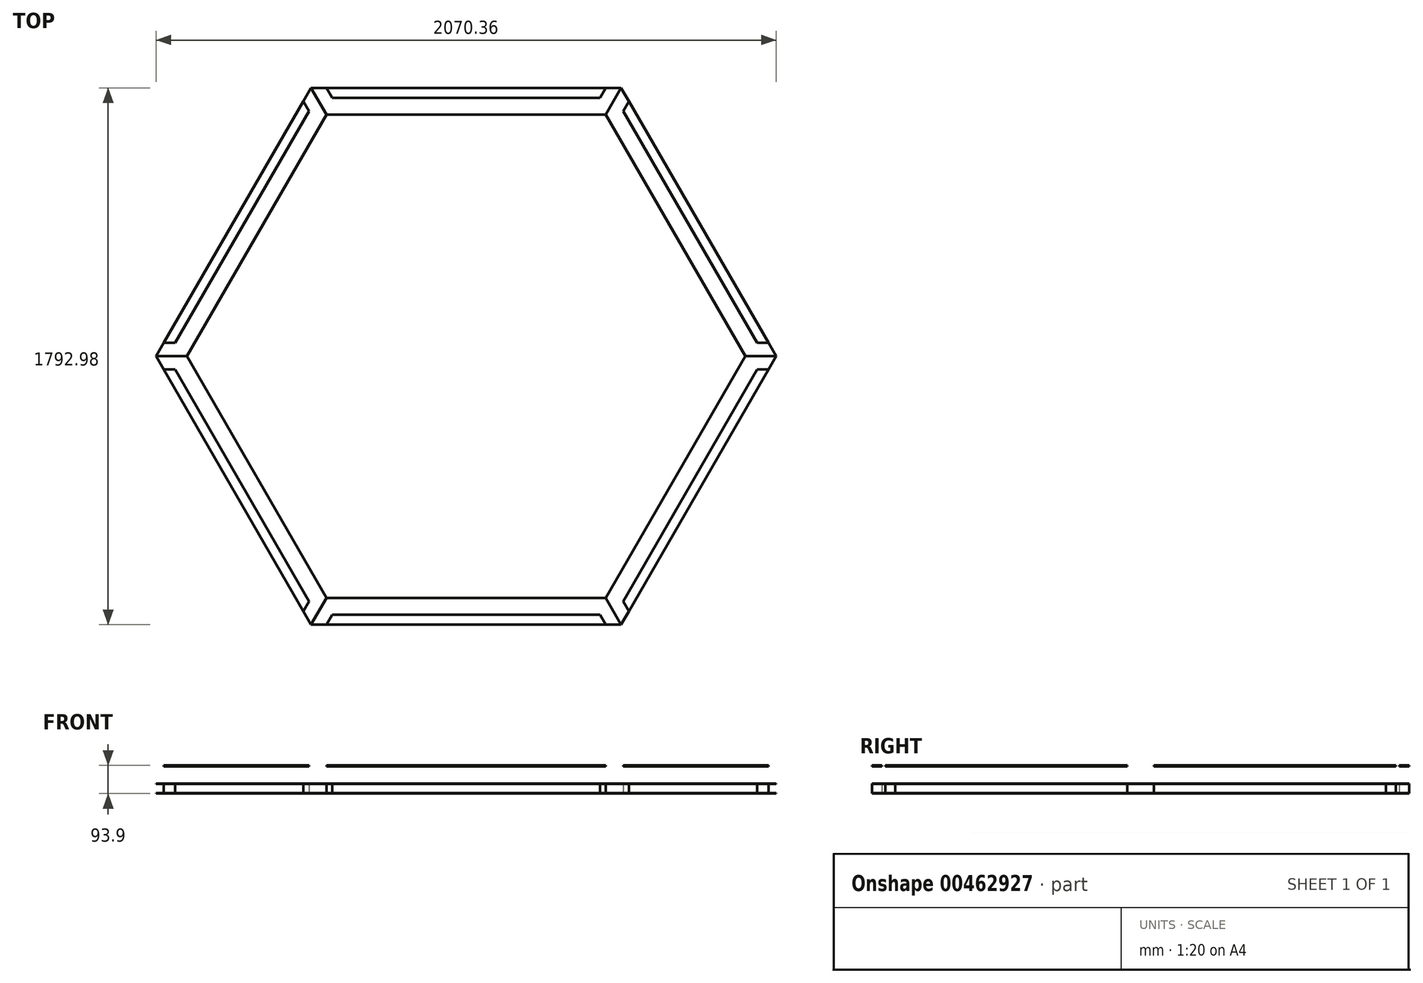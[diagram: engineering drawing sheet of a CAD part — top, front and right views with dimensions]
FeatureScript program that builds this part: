
annotation { "Feature Type Name" : "Feature", "Feature Type Description" : "" }
export const myFeature = defineFeature(function(context is Context, id is Id, definition is map)
    precondition{}
    {
        {
            assignVariable(context, id + "F0", {"name" : "t2", "anyValue" : 1.5});
        }
        {
            assignVariable(context, id + "F1", {"name" : "w2", "anyValue" : 3.5});
        }
        {
            assignVariable(context, id + "F2", {"name" : "ash", "anyValue" : 34});
        }
        {
            assignVariable(context, id + "F3", {"name" : "asupright", "anyValue" : getVariable(context, 'ash') - getVariable(context, 't2') * 2});
        }
        {
            var Q0;
            Q0=qCreatedBy(makeId("Top.planeOp"),FACE);
            var sketch = newSketch(context, id + "F4", { "sketchPlane" : qUnion([Q0])});
            skCircle(sketch, "E0.cCircle", {"center": v(0, 0) * mm, "radius": 896.5 * mm, "construction": true});
            skLineSegment(sketch, "E0.0", {"start": v(-517.6, 896.5) * mm, "end": v(517.6, 896.5) * mm});
            skLineSegment(sketch, "E0.1", {"start": v(517.6, 896.5) * mm, "end": v(1035.18, 0) * mm});
            skLineSegment(sketch, "E0.2", {"start": v(1035.18, 0) * mm, "end": v(517.6, -896.5) * mm});
            skLineSegment(sketch, "E0.3", {"start": v(517.6, -896.5) * mm, "end": v(-517.6, -896.5) * mm});
            skLineSegment(sketch, "E0.4", {"start": v(-517.6, -896.5) * mm, "end": v(-1035.18, 0) * mm});
            skLineSegment(sketch, "E0.5", {"start": v(-1035.18, 0) * mm, "end": v(-517.6, 896.5) * mm});
            skPoint(sketch, "E0.0.midPoint", {"position": v(0, 896.5) * mm});
            skLineSegment(sketch, "E1.0", {"start": v(-932.53, 0) * mm, "end": v(-466.26, 807.6) * mm});
            skLineSegment(sketch, "E1.1", {"start": v(466.26, 807.6) * mm, "end": v(932.53, 0) * mm});
            skLineSegment(sketch, "E1.2", {"start": v(932.53, 0) * mm, "end": v(466.26, -807.6) * mm});
            skLineSegment(sketch, "E1.3", {"start": v(-466.26, 807.6) * mm, "end": v(466.26, 807.6) * mm});
            skLineSegment(sketch, "E1.4", {"start": v(466.26, -807.6) * mm, "end": v(-466.26, -807.6) * mm});
            skLineSegment(sketch, "E1.5", {"start": v(-466.26, -807.6) * mm, "end": v(-932.53, 0) * mm});
            skLineSegment(sketch, "E2", {"start": v(-517.6, 896.5) * mm, "end": v(-466.26, 807.6) * mm});
            skLineSegment(sketch, "E3", {"start": v(517.6, 896.5) * mm, "end": v(466.26, 807.6) * mm});
            skLineSegment(sketch, "E4", {"start": v(1035.18, 0) * mm, "end": v(932.53, 0) * mm});
            skLineSegment(sketch, "E5", {"start": v(517.6, -896.5) * mm, "end": v(466.26, -807.6) * mm});
            skLineSegment(sketch, "E6", {"start": v(-466.26, -807.6) * mm, "end": v(-517.6, -896.5) * mm});
            skLineSegment(sketch, "E7", {"start": v(-932.53, 0) * mm, "end": v(-1035.18, 0) * mm});
            skSolve(sketch);
        }
        {
            var Q0;
            Q0=makeQuery(id+"F4.imprint","IMPRINT",FACE,{"disambiguationData":[TD([[makeQuery(id+"F4.imprint","IMPRINT",EDGE,{"derivedFrom":sQuery(id+"F4.wireOp",EDGE,"E0.5")}),-1.0]])]});
            extrude(context, id + "F5", {"entities" : qUnion([Q0]), "depth" : (getVariable(context, 't2')) * mm});
        }
        {
            var Q0;
            Q0=makeQuery(id+"F4.imprint","IMPRINT",FACE,{"disambiguationData":[TD([[makeQuery(id+"F4.imprint","IMPRINT",EDGE,{"derivedFrom":sQuery(id+"F4.wireOp",EDGE,"E0.0")}),-1.0]])]});
            extrude(context, id + "F6", {"entities" : qUnion([Q0]), "depth" : (getVariable(context, 't2')) * mm});
        }
        {
            var Q0;
            Q0=makeQuery(id+"F4.imprint","IMPRINT",FACE,{"disambiguationData":[TD([[makeQuery(id+"F4.imprint","IMPRINT",EDGE,{"derivedFrom":sQuery(id+"F4.wireOp",EDGE,"E0.1")}),-1.0]])]});
            extrude(context, id + "F7", {"entities" : qUnion([Q0]), "depth" : (getVariable(context, 't2')) * mm});
        }
        {
            var Q0;
            Q0=makeQuery(id+"F4.imprint","IMPRINT",FACE,{"disambiguationData":[TD([[makeQuery(id+"F4.imprint","IMPRINT",EDGE,{"derivedFrom":sQuery(id+"F4.wireOp",EDGE,"E0.2")}),-1.0]])]});
            extrude(context, id + "F8", {"entities" : qUnion([Q0]), "depth" : (getVariable(context, 't2')) * mm});
        }
        {
            var Q0;
            Q0=makeQuery(id+"F4.imprint","IMPRINT",FACE,{"disambiguationData":[TD([[makeQuery(id+"F4.imprint","IMPRINT",EDGE,{"derivedFrom":sQuery(id+"F4.wireOp",EDGE,"E0.3")}),-1.0]])]});
            extrude(context, id + "F9", {"entities" : qUnion([Q0]), "depth" : (getVariable(context, 't2')) * mm});
        }
        {
            var Q0;
            Q0=makeQuery(id+"F4.imprint","IMPRINT",FACE,{"disambiguationData":[TD([[makeQuery(id+"F4.imprint","IMPRINT",EDGE,{"derivedFrom":sQuery(id+"F4.wireOp",EDGE,"E0.4")}),-1.0]])]});
            extrude(context, id + "F10", {"entities" : qUnion([Q0]), "depth" : (getVariable(context, 't2')) * mm});
        }
        {
            var Q0;
            Q0=makeQuery(id+"F5.opExtrude","CAP_FACE",FACE,{"disambiguationData":[OSD([sQuery(id+"F4.wireOp",EDGE,"E0.5"),sQuery(id+"F4.wireOp",EDGE,"E1.0"),sQuery(id+"F4.wireOp",EDGE,"E2"),sQuery(id+"F4.wireOp",EDGE,"E7")])],"isStart":false});
            var sketch = newSketch(context, id + "F11", { "sketchPlane" : qUnion([Q0])});
            skLineSegment(sketch, "E8.0", {"start": v(-517.6, -896.5) * mm, "end": v(-1035.18, 0) * mm, "construction": true});
            skLineSegment(sketch, "E8.1", {"start": v(-1035.18, 0) * mm, "end": v(-517.6, 896.5) * mm, "construction": true});
            skLineSegment(sketch, "E9.0", {"start": v(-517.6, 896.5) * mm, "end": v(517.6, 896.5) * mm, "construction": true});
            skLineSegment(sketch, "E9.1", {"start": v(517.6, 896.5) * mm, "end": v(1035.18, 0) * mm, "construction": true});
            skLineSegment(sketch, "E9.2", {"start": v(1035.18, 0) * mm, "end": v(517.6, -896.5) * mm, "construction": true});
            skLineSegment(sketch, "E9.3", {"start": v(517.6, -896.5) * mm, "end": v(-517.6, -896.5) * mm, "construction": true});
            skLineSegment(sketch, "E10.bottom", {"start": v(-1009.52, 44.45) * mm, "end": v(-971.42, 44.45) * mm});
            skLineSegment(sketch, "E10.top", {"start": v(-1009.52, -44.45) * mm, "end": v(-971.42, -44.45) * mm});
            skLineSegment(sketch, "E10.left", {"start": v(-1009.52, 44.45) * mm, "end": v(-1009.52, -44.45) * mm});
            skLineSegment(sketch, "E10.right", {"start": v(-971.42, 44.45) * mm, "end": v(-971.42, -44.45) * mm});
            skLineSegment(sketch, "E11.1.0", {"start": v(-543.25, -852.04) * mm, "end": v(-524.2, -819.05) * mm});
            skLineSegment(sketch, "E11.1.1", {"start": v(-524.2, -819.05) * mm, "end": v(-447.21, -863.5) * mm});
            skLineSegment(sketch, "E11.1.2", {"start": v(-466.26, -896.5) * mm, "end": v(-447.21, -863.5) * mm});
            skLineSegment(sketch, "E11.1.3", {"start": v(-543.25, -852.04) * mm, "end": v(-466.26, -896.5) * mm});
            skLineSegment(sketch, "E11.2.0", {"start": v(466.26, -896.5) * mm, "end": v(447.21, -863.5) * mm});
            skLineSegment(sketch, "E11.2.1", {"start": v(447.21, -863.5) * mm, "end": v(524.2, -819.05) * mm});
            skLineSegment(sketch, "E11.2.2", {"start": v(543.25, -852.04) * mm, "end": v(524.2, -819.05) * mm});
            skLineSegment(sketch, "E11.2.3", {"start": v(466.26, -896.5) * mm, "end": v(543.25, -852.04) * mm});
            skLineSegment(sketch, "E11.3.0", {"start": v(1009.52, -44.45) * mm, "end": v(971.42, -44.45) * mm});
            skLineSegment(sketch, "E11.3.1", {"start": v(971.42, -44.45) * mm, "end": v(971.42, 44.45) * mm});
            skLineSegment(sketch, "E11.3.2", {"start": v(1009.52, 44.45) * mm, "end": v(971.42, 44.45) * mm});
            skLineSegment(sketch, "E11.3.3", {"start": v(1009.52, -44.45) * mm, "end": v(1009.52, 44.45) * mm});
            skLineSegment(sketch, "E11.4.0", {"start": v(543.25, 852.04) * mm, "end": v(524.2, 819.05) * mm});
            skLineSegment(sketch, "E11.4.1", {"start": v(524.2, 819.05) * mm, "end": v(447.21, 863.5) * mm});
            skLineSegment(sketch, "E11.4.2", {"start": v(466.26, 896.5) * mm, "end": v(447.21, 863.5) * mm});
            skLineSegment(sketch, "E11.4.3", {"start": v(543.25, 852.04) * mm, "end": v(466.26, 896.5) * mm});
            skLineSegment(sketch, "E11.5.0", {"start": v(-466.26, 896.5) * mm, "end": v(-447.21, 863.5) * mm});
            skLineSegment(sketch, "E11.5.1", {"start": v(-447.21, 863.5) * mm, "end": v(-524.2, 819.05) * mm});
            skLineSegment(sketch, "E11.5.2", {"start": v(-543.25, 852.04) * mm, "end": v(-524.2, 819.05) * mm});
            skLineSegment(sketch, "E11.5.3", {"start": v(-466.26, 896.5) * mm, "end": v(-543.25, 852.04) * mm});
            skPoint(sketch, "E11.center", {"position": v(0, 0) * mm});
            skLineSegment(sketch, "E12", {"start": v(-466.26, -896.5) * mm, "end": v(466.26, -896.5) * mm});
            skLineSegment(sketch, "E13", {"start": v(-447.21, -863.5) * mm, "end": v(447.21, -863.5) * mm});
            skLineSegment(sketch, "E14", {"start": v(543.25, -852.04) * mm, "end": v(1009.52, -44.45) * mm});
            skLineSegment(sketch, "E15", {"start": v(971.42, -44.45) * mm, "end": v(524.2, -819.05) * mm});
            skLineSegment(sketch, "E16", {"start": v(971.42, 44.45) * mm, "end": v(524.2, 819.05) * mm});
            skLineSegment(sketch, "E17", {"start": v(543.25, 852.04) * mm, "end": v(1009.52, 44.45) * mm});
            skLineSegment(sketch, "E18", {"start": v(447.21, 863.5) * mm, "end": v(-447.21, 863.5) * mm});
            skLineSegment(sketch, "E19", {"start": v(-466.26, 896.5) * mm, "end": v(466.26, 896.5) * mm});
            skLineSegment(sketch, "E20", {"start": v(-543.25, 852.04) * mm, "end": v(-1009.52, 44.45) * mm});
            skLineSegment(sketch, "E21", {"start": v(-971.42, 44.45) * mm, "end": v(-524.2, 819.05) * mm});
            skLineSegment(sketch, "E22", {"start": v(-1009.52, -44.45) * mm, "end": v(-543.25, -852.04) * mm});
            skLineSegment(sketch, "E23", {"start": v(-524.2, -819.05) * mm, "end": v(-971.42, -44.45) * mm});
            skSolve(sketch);
        }
        {
            var Q0;
            {var subQ0=sQuery(id+"F11.wireOp",EDGE,"E10.bottom");Q0=makeQuery(id+"F11.imprint","IMPRINT",FACE,{"disambiguationData":[TD([[makeQuery(id+"F11.imprint","IMPRINT",EDGE,{"derivedFrom":subQ0}),-1.0]])]});}
            var Q1;
            {var subQ0=sQuery(id+"F11.wireOp",EDGE,"E10.top");Q1=makeQuery(id+"F11.imprint","IMPRINT",FACE,{"disambiguationData":[TD([[makeQuery(id+"F11.imprint","IMPRINT",EDGE,{"derivedFrom":subQ0}),1.0]])]});}
            extrude(context, id + "F12", {"entities" : qUnion([Q0, Q1]), "depth" : (getVariable(context, 'asupright')) * mm});
        }
        {
            var Q0;
            {var subQ0=sQuery(id+"F11.wireOp",EDGE,"E11.5.2");Q0=makeQuery(id+"F11.imprint","IMPRINT",FACE,{"disambiguationData":[TD([[makeQuery(id+"F11.imprint","IMPRINT",EDGE,{"derivedFrom":subQ0}),1.0]])]});}
            var Q1;
            {var subQ0=sQuery(id+"F11.wireOp",EDGE,"E11.5.0");Q1=makeQuery(id+"F11.imprint","IMPRINT",FACE,{"disambiguationData":[TD([[makeQuery(id+"F11.imprint","IMPRINT",EDGE,{"derivedFrom":subQ0}),-1.0]])]});}
            extrude(context, id + "F13", {"entities" : qUnion([Q0, Q1]), "depth" : (getVariable(context, 'asupright')) * mm});
        }
        {
            var Q0;
            Q0=makeQuery(id+"F11.imprint","IMPRINT",FACE,{"disambiguationData":[TD([[makeQuery(id+"F11.imprint","IMPRINT",EDGE,{"derivedFrom":sQuery(id+"F11.wireOp",EDGE,"E11.4.0")}),-1.0]])]});
            extrude(context, id + "F14", {"entities" : qUnion([Q0]), "depth" : (getVariable(context, 'asupright')) * mm});
        }
        {
            var Q0;
            Q0=makeQuery(id+"F11.imprint","IMPRINT",FACE,{"disambiguationData":[TD([[makeQuery(id+"F11.imprint","IMPRINT",EDGE,{"derivedFrom":sQuery(id+"F11.wireOp",EDGE,"E11.3.0")}),-1.0]])]});
            extrude(context, id + "F15", {"entities" : qUnion([Q0]), "depth" : (getVariable(context, 'asupright')) * mm});
        }
        {
            var Q0;
            Q0=makeQuery(id+"F11.imprint","IMPRINT",FACE,{"disambiguationData":[TD([[makeQuery(id+"F11.imprint","IMPRINT",EDGE,{"derivedFrom":sQuery(id+"F11.wireOp",EDGE,"E11.2.0")}),-1.0]])]});
            extrude(context, id + "F16", {"entities" : qUnion([Q0]), "depth" : (getVariable(context, 'asupright')) * mm});
        }
        {
            var Q0;
            Q0=makeQuery(id+"F11.imprint","IMPRINT",FACE,{"disambiguationData":[TD([[makeQuery(id+"F11.imprint","IMPRINT",EDGE,{"derivedFrom":sQuery(id+"F11.wireOp",EDGE,"E11.1.0")}),-1.0]])]});
            extrude(context, id + "F17", {"entities" : qUnion([Q0]), "depth" : (getVariable(context, 'asupright')) * mm});
        }
        {
            var Q0;
            Q0=makeQuery(id+"F11.imprint","IMPRINT",FACE,{"disambiguationData":[TD([[makeQuery(id+"F11.imprint","IMPRINT",EDGE,{"derivedFrom":sQuery(id+"F11.wireOp",EDGE,"E11.1.2")}),-1.0]])]});
            extrude(context, id + "F18", {"entities" : qUnion([Q0]), "depth" : (getVariable(context, 'w2')) * mm});
        }
        {
            var Q0;
            Q0=makeQuery(id+"F11.imprint","IMPRINT",FACE,{"disambiguationData":[TD([[makeQuery(id+"F11.imprint","IMPRINT",EDGE,{"derivedFrom":sQuery(id+"F11.wireOp",EDGE,"E11.2.2")}),-1.0]])]});
            extrude(context, id + "F19", {"entities" : qUnion([Q0]), "depth" : (getVariable(context, 'w2')) * mm});
        }
        {
            var Q0;
            Q0=makeQuery(id+"F11.imprint","IMPRINT",FACE,{"disambiguationData":[TD([[makeQuery(id+"F11.imprint","IMPRINT",EDGE,{"derivedFrom":sQuery(id+"F11.wireOp",EDGE,"E11.3.2")}),-1.0]])]});
            extrude(context, id + "F20", {"entities" : qUnion([Q0]), "depth" : (getVariable(context, 'w2')) * mm});
        }
        {
            var Q0;
            Q0=makeQuery(id+"F11.imprint","IMPRINT",FACE,{"disambiguationData":[TD([[makeQuery(id+"F11.imprint","IMPRINT",EDGE,{"derivedFrom":sQuery(id+"F11.wireOp",EDGE,"E11.4.2")}),-1.0]])]});
            extrude(context, id + "F21", {"entities" : qUnion([Q0]), "depth" : (getVariable(context, 'w2')) * mm});
        }
        {
            var Q0;
            Q0=makeQuery(id+"F11.imprint","IMPRINT",FACE,{"disambiguationData":[TD([[makeQuery(id+"F11.imprint","IMPRINT",EDGE,{"derivedFrom":sQuery(id+"F11.wireOp",EDGE,"E10.bottom")}),1.0]])]});
            extrude(context, id + "F22", {"entities" : qUnion([Q0]), "depth" : (getVariable(context, 'w2')) * mm});
        }
        {
            var Q0;
            Q0=makeQuery(id+"F11.imprint","IMPRINT",FACE,{"disambiguationData":[TD([[makeQuery(id+"F11.imprint","IMPRINT",EDGE,{"derivedFrom":sQuery(id+"F11.wireOp",EDGE,"E10.top")}),-1.0]])]});
            extrude(context, id + "F23", {"entities" : qUnion([Q0]), "depth" : (getVariable(context, 'w2')) * mm});
        }
        {
            var Q0;
            Q0=makeQuery(id+"F23.opExtrude","SWEPT_BODY",BODY,{"disambiguationData":[OSD([sQuery(id+"F11.wireOp",EDGE,"E10.top"),sQuery(id+"F11.wireOp",EDGE,"E11.1.0"),sQuery(id+"F11.wireOp",EDGE,"E22"),sQuery(id+"F11.wireOp",EDGE,"E23")])]});
            var Q1;
            Q1=makeQuery(id+"F22.opExtrude","SWEPT_BODY",BODY,{"disambiguationData":[OSD([sQuery(id+"F11.wireOp",EDGE,"E10.bottom"),sQuery(id+"F11.wireOp",EDGE,"E11.5.2"),sQuery(id+"F11.wireOp",EDGE,"E20"),sQuery(id+"F11.wireOp",EDGE,"E21")])]});
            var Q2;
            Q2=makeQuery(id+"F21.opExtrude","SWEPT_BODY",BODY,{"disambiguationData":[OSD([sQuery(id+"F11.wireOp",EDGE,"E11.4.2"),sQuery(id+"F11.wireOp",EDGE,"E11.5.0"),sQuery(id+"F11.wireOp",EDGE,"E18"),sQuery(id+"F11.wireOp",EDGE,"E19")])]});
            var Q3;
            Q3=makeQuery(id+"F20.opExtrude","SWEPT_BODY",BODY,{"disambiguationData":[OSD([sQuery(id+"F11.wireOp",EDGE,"E11.3.2"),sQuery(id+"F11.wireOp",EDGE,"E11.4.0"),sQuery(id+"F11.wireOp",EDGE,"E16"),sQuery(id+"F11.wireOp",EDGE,"E17")])]});
            var Q4;
            Q4=makeQuery(id+"F19.opExtrude","SWEPT_BODY",BODY,{"disambiguationData":[OSD([sQuery(id+"F11.wireOp",EDGE,"E11.2.2"),sQuery(id+"F11.wireOp",EDGE,"E11.3.0"),sQuery(id+"F11.wireOp",EDGE,"E14"),sQuery(id+"F11.wireOp",EDGE,"E15")])]});
            var Q5;
            Q5=makeQuery(id+"F18.opExtrude","SWEPT_BODY",BODY,{"disambiguationData":[OSD([sQuery(id+"F11.wireOp",EDGE,"E11.1.2"),sQuery(id+"F11.wireOp",EDGE,"E11.2.0"),sQuery(id+"F11.wireOp",EDGE,"E12"),sQuery(id+"F11.wireOp",EDGE,"E13")])]});
            transform(context, id + "F24", {"entities" : qUnion([Q0, Q1, Q2, Q3, Q4, Q5]), "transformType" : TransformType.TRANSLATION_3D, "dx" : 0 * mm, "dy" : 0 * mm, "dz" : 88.9 * mm, "makeCopy" : false});
        }
        {
            var Q0;
            Q0=makeQuery(id+"F5.opExtrude","SWEPT_BODY",BODY,{"disambiguationData":[OSD([sQuery(id+"F4.wireOp",EDGE,"E0.5"),sQuery(id+"F4.wireOp",EDGE,"E1.0"),sQuery(id+"F4.wireOp",EDGE,"E2"),sQuery(id+"F4.wireOp",EDGE,"E7")])]});
            var Q1;
            Q1=makeQuery(id+"F6.opExtrude","SWEPT_BODY",BODY,{"disambiguationData":[OSD([sQuery(id+"F4.wireOp",EDGE,"E0.0"),sQuery(id+"F4.wireOp",EDGE,"E1.3"),sQuery(id+"F4.wireOp",EDGE,"E2"),sQuery(id+"F4.wireOp",EDGE,"E3")])]});
            var Q2;
            Q2=makeQuery(id+"F7.opExtrude","SWEPT_BODY",BODY,{"disambiguationData":[OSD([sQuery(id+"F4.wireOp",EDGE,"E0.1"),sQuery(id+"F4.wireOp",EDGE,"E1.1"),sQuery(id+"F4.wireOp",EDGE,"E3"),sQuery(id+"F4.wireOp",EDGE,"E4")])]});
            var Q3;
            Q3=makeQuery(id+"F8.opExtrude","SWEPT_BODY",BODY,{"disambiguationData":[OSD([sQuery(id+"F4.wireOp",EDGE,"E0.2"),sQuery(id+"F4.wireOp",EDGE,"E1.2"),sQuery(id+"F4.wireOp",EDGE,"E4"),sQuery(id+"F4.wireOp",EDGE,"E5")])]});
            var Q4;
            Q4=makeQuery(id+"F9.opExtrude","SWEPT_BODY",BODY,{"disambiguationData":[OSD([sQuery(id+"F4.wireOp",EDGE,"E0.3"),sQuery(id+"F4.wireOp",EDGE,"E1.4"),sQuery(id+"F4.wireOp",EDGE,"E5"),sQuery(id+"F4.wireOp",EDGE,"E6")])]});
            var Q5;
            Q5=makeQuery(id+"F10.opExtrude","SWEPT_BODY",BODY,{"disambiguationData":[OSD([sQuery(id+"F4.wireOp",EDGE,"E0.4"),sQuery(id+"F4.wireOp",EDGE,"E1.5"),sQuery(id+"F4.wireOp",EDGE,"E6"),sQuery(id+"F4.wireOp",EDGE,"E7")])]});
            transform(context, id + "F25", {"entities" : qUnion([Q0, Q1, Q2, Q3, Q4, Q5]), "transformType" : TransformType.TRANSLATION_3D, "dx" : 0 * mm, "dy" : 0 * mm, "dz" : (getVariable(context, 'ash') - getVariable(context, 't2')) * mm, "makeCopy" : true});
        }
    });
